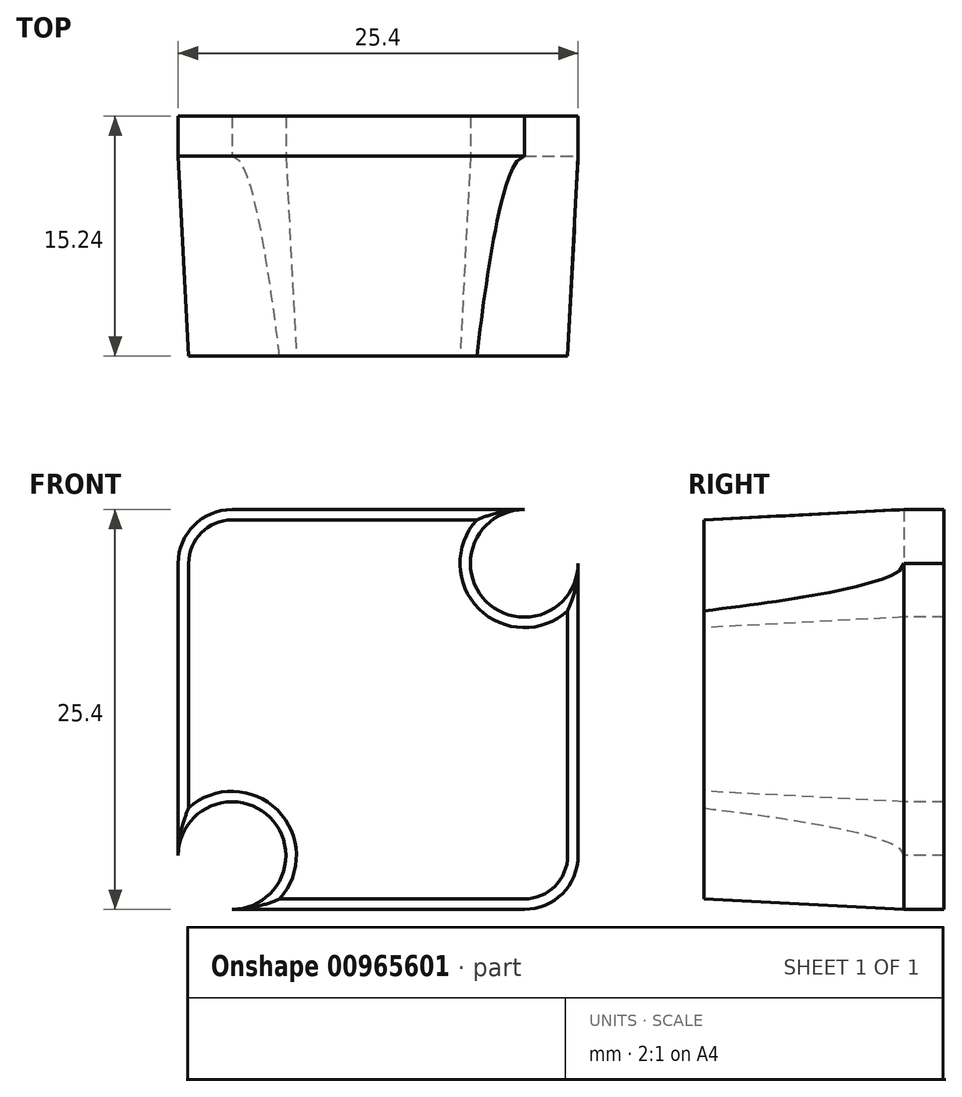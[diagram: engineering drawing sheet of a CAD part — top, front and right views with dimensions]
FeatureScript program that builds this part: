
annotation { "Feature Type Name" : "Feature", "Feature Type Description" : "" }
export const myFeature = defineFeature(function(context is Context, id is Id, definition is map)
    precondition{}
    {
        {
            var Q0;
            Q0=qCreatedBy(makeId("Front.planeOp"),FACE);
            var sketch = newSketch(context, id + "F0", { "sketchPlane" : qUnion([Q0])});
            skLineSegment(sketch, "E0.bottom", {"start": v(-12.7, 12.7) * mm, "end": v(12.7, 12.7) * mm});
            skLineSegment(sketch, "E0.top", {"start": v(-12.7, -12.7) * mm, "end": v(12.7, -12.7) * mm});
            skLineSegment(sketch, "E0.left", {"start": v(-12.7, 12.7) * mm, "end": v(-12.7, -12.7) * mm});
            skLineSegment(sketch, "E0.right", {"start": v(12.7, 12.7) * mm, "end": v(12.7, -12.7) * mm});
            skCircle(sketch, "E1", {"center": v(-9.28, 9.28) * mm, "radius": 3.42 * mm});
            skCircle(sketch, "E2.MirrorC", {"center": v(9.28, 9.28) * mm, "radius": 3.42 * mm});
            skCircle(sketch, "E3.MirrorC", {"center": v(-9.28, -9.28) * mm, "radius": 3.42 * mm});
            skCircle(sketch, "E4.MirrorC", {"center": v(9.28, -9.28) * mm, "radius": 3.42 * mm});
            skSolve(sketch);
        }
        {
            var Q0;
            {var subQ5=sQuery(id+"F0.wireOp",EDGE,"E1");var subQ13=sQuery(id+"F0.wireOp",EDGE,"E0.bottom");var subQ15=makeQuery(id+"F0.imprint","INTERSECT",VERTEX,{"derivedFrom":[subQ13,subQ5]});Q0=makeQuery(id+"F0.imprint","IMPRINT",FACE,{"disambiguationData":[TD([[makeQuery(id+"F0.imprint","IMPRINT",EDGE,{"disambiguationData":[TD([[subQ15,-1.0]])],"derivedFrom":subQ13}),-1.0]])]});}
            var Q1;
            {var subQ0=sQuery(id+"F0.wireOp",EDGE,"E1");var subQ1=makeQuery(id+"F0.imprint","INTERSECT",VERTEX,{"derivedFrom":[sQuery(id+"F0.wireOp",EDGE,"E0.bottom"),subQ0]});Q1=makeQuery(id+"F0.imprint","IMPRINT",FACE,{"disambiguationData":[TD([[makeQuery(id+"F0.imprint","IMPRINT",EDGE,{"disambiguationData":[TD([[subQ1,-1.0]])],"derivedFrom":subQ0}),1.0]])]});}
            var Q2;
            {var subQ0=sQuery(id+"F0.wireOp",EDGE,"E2.MirrorC");var subQ1=makeQuery(id+"F0.imprint","INTERSECT",VERTEX,{"derivedFrom":[sQuery(id+"F0.wireOp",EDGE,"E0.bottom"),subQ0]});Q2=makeQuery(id+"F0.imprint","IMPRINT",FACE,{"disambiguationData":[TD([[makeQuery(id+"F0.imprint","IMPRINT",EDGE,{"disambiguationData":[TD([[subQ1,-1.0]])],"derivedFrom":subQ0}),-1.0]])]});}
            var Q3;
            {var subQ0=sQuery(id+"F0.wireOp",EDGE,"E4.MirrorC");var subQ1=makeQuery(id+"F0.imprint","INTERSECT",VERTEX,{"derivedFrom":[sQuery(id+"F0.wireOp",EDGE,"E0.top"),subQ0]});Q3=makeQuery(id+"F0.imprint","IMPRINT",FACE,{"disambiguationData":[TD([[makeQuery(id+"F0.imprint","IMPRINT",EDGE,{"disambiguationData":[TD([[subQ1,-1.0]])],"derivedFrom":subQ0}),1.0]])]});}
            var Q4;
            {var subQ0=sQuery(id+"F0.wireOp",EDGE,"E3.MirrorC");var subQ1=makeQuery(id+"F0.imprint","INTERSECT",VERTEX,{"derivedFrom":[sQuery(id+"F0.wireOp",EDGE,"E0.top"),subQ0]});Q4=makeQuery(id+"F0.imprint","IMPRINT",FACE,{"disambiguationData":[TD([[makeQuery(id+"F0.imprint","IMPRINT",EDGE,{"disambiguationData":[TD([[subQ1,-1.0]])],"derivedFrom":subQ0}),-1.0]])]});}
            extrude(context, id + "F1", {"entities" : qUnion([Q0, Q1, Q2, Q3, Q4]), "oppositeDirection" : true, "depth" : 2.54 * mm, "offsetDistance" : 25.4 * mm});
        }
        {
            var Q0;
            {var subQ0=sQuery(id+"F0.wireOp",EDGE,"E1");var subQ1=makeQuery(id+"F0.imprint","INTERSECT",VERTEX,{"derivedFrom":[sQuery(id+"F0.wireOp",EDGE,"E0.bottom"),subQ0]});Q0=makeQuery(id+"F0.imprint","IMPRINT",FACE,{"disambiguationData":[TD([[makeQuery(id+"F0.imprint","IMPRINT",EDGE,{"disambiguationData":[TD([[subQ1,-1.0]])],"derivedFrom":subQ0}),1.0]])]});}
            var Q1;
            {var subQ0=sQuery(id+"F0.wireOp",EDGE,"E2.MirrorC");var subQ1=makeQuery(id+"F0.imprint","INTERSECT",VERTEX,{"derivedFrom":[sQuery(id+"F0.wireOp",EDGE,"E0.bottom"),subQ0]});Q1=makeQuery(id+"F0.imprint","IMPRINT",FACE,{"disambiguationData":[TD([[makeQuery(id+"F0.imprint","IMPRINT",EDGE,{"disambiguationData":[TD([[subQ1,-1.0]])],"derivedFrom":subQ0}),-1.0]])]});}
            var Q2;
            {var subQ0=sQuery(id+"F0.wireOp",EDGE,"E4.MirrorC");var subQ1=makeQuery(id+"F0.imprint","INTERSECT",VERTEX,{"derivedFrom":[sQuery(id+"F0.wireOp",EDGE,"E0.top"),subQ0]});Q2=makeQuery(id+"F0.imprint","IMPRINT",FACE,{"disambiguationData":[TD([[makeQuery(id+"F0.imprint","IMPRINT",EDGE,{"disambiguationData":[TD([[subQ1,-1.0]])],"derivedFrom":subQ0}),1.0]])]});}
            var Q3;
            {var subQ0=sQuery(id+"F0.wireOp",EDGE,"E3.MirrorC");var subQ1=makeQuery(id+"F0.imprint","INTERSECT",VERTEX,{"derivedFrom":[sQuery(id+"F0.wireOp",EDGE,"E0.top"),subQ0]});Q3=makeQuery(id+"F0.imprint","IMPRINT",FACE,{"disambiguationData":[TD([[makeQuery(id+"F0.imprint","IMPRINT",EDGE,{"disambiguationData":[TD([[subQ1,-1.0]])],"derivedFrom":subQ0}),-1.0]])]});}
            extrude(context, id + "F2", {"entities" : qUnion([Q0, Q1, Q2, Q3]), "operationType" : NewBodyOperationType.ADD, "depth" : 12.7 * mm, "offsetDistance" : 25.4 * mm, "hasDraft" : true, "draftAngle" : 3 * degree, "draftPullDirection" : true});
        }
    });
